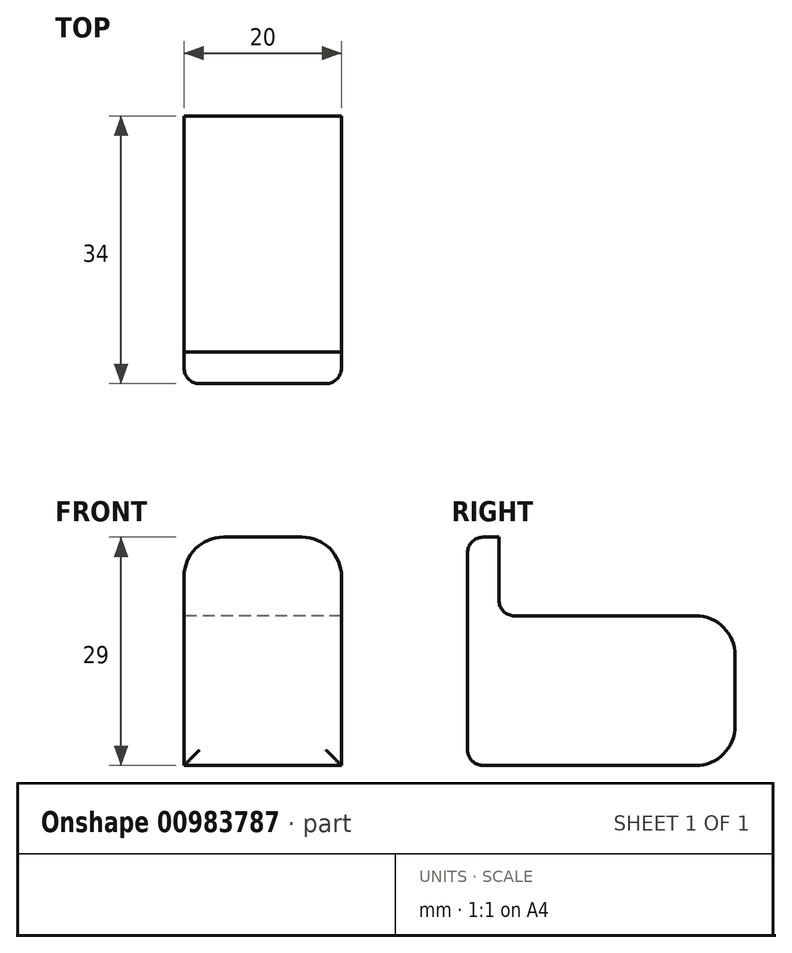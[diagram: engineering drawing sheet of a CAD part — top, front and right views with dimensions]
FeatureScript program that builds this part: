
annotation { "Feature Type Name" : "Feature", "Feature Type Description" : "" }
export const myFeature = defineFeature(function(context is Context, id is Id, definition is map)
    precondition{}
    {
        {
            var Q0;
            Q0=qCreatedBy(makeId("Right.planeOp"),FACE);
            var sketch = newSketch(context, id + "F0", { "sketchPlane" : qUnion([Q0])});
            skLineSegment(sketch, "E0", {"start": v(-17, 0) * mm, "end": v(-17, 29) * mm});
            skLineSegment(sketch, "E1", {"start": v(-17, 29) * mm, "end": v(-13, 29) * mm});
            skLineSegment(sketch, "E2", {"start": v(-13, 29) * mm, "end": v(-13, 19) * mm});
            skLineSegment(sketch, "E3", {"start": v(-13, 19) * mm, "end": v(17, 19) * mm});
            skLineSegment(sketch, "E4", {"start": v(17, 19) * mm, "end": v(17, 0) * mm});
            skLineSegment(sketch, "E5", {"start": v(17, 0) * mm, "end": v(-17, 0) * mm});
            skSolve(sketch);
        }
        {
            var Q0;
            Q0=makeQuery(id+"F0.imprint","IMPRINT",FACE,{"disambiguationData":[TD([[makeQuery(id+"F0.imprint","IMPRINT",EDGE,{"derivedFrom":sQuery(id+"F0.wireOp",EDGE,"E0")}),-1.0]])]});
            extrude(context, id + "F1", {"entities" : qUnion([Q0]), "depth" : 20 * mm, "offsetDistance" : 25 * mm});
        }
        {
            var Q0;
            Q0=makeQuery(id+"F1.opExtrude","CAP_EDGE",EDGE,{"disambiguationData":[OSD([sQuery(id+"F0.wireOp",EDGE,"E1")])],"isStart":false});
            var Q1;
            Q1=makeQuery(id+"F1.opExtrude","CAP_EDGE",EDGE,{"disambiguationData":[OSD([sQuery(id+"F0.wireOp",EDGE,"E1")])],"isStart":true});
            var Q2;
            Q2=makeQuery(id+"F1.opExtrude","SWEPT_EDGE",EDGE,{"disambiguationData":[OSD([sQuery(id+"F0.wireOp",EDGE,"E3"),sQuery(id+"F0.wireOp",EDGE,"E4")])]});
            var Q3;
            Q3=makeQuery(id+"F1.opExtrude","SWEPT_EDGE",EDGE,{"disambiguationData":[OSD([sQuery(id+"F0.wireOp",EDGE,"E4"),sQuery(id+"F0.wireOp",EDGE,"E5")])]});
            fillet(context, id + "F2", {"entities" : qUnion([Q0, Q1, Q2, Q3]), "radius" : 5 * mm, "tangentPropagation" : true, "allowEdgeOverflow" : false});
        }
        {
            var Q0;
            Q0=makeQuery(id+"F1.opExtrude","SWEPT_EDGE",EDGE,{"disambiguationData":[OSD([sQuery(id+"F0.wireOp",EDGE,"E0"),sQuery(id+"F0.wireOp",EDGE,"E5")])]});
            var Q1;
            Q1=makeQuery(id+"F1.opExtrude","SWEPT_EDGE",EDGE,{"disambiguationData":[OSD([sQuery(id+"F0.wireOp",EDGE,"E0"),sQuery(id+"F0.wireOp",EDGE,"E1")])]});
            var Q2;
            Q2=makeQuery(id+"F1.opExtrude","SWEPT_EDGE",EDGE,{"disambiguationData":[OSD([sQuery(id+"F0.wireOp",EDGE,"E2"),sQuery(id+"F0.wireOp",EDGE,"E3")])]});
            fillet(context, id + "F3", {"entities" : qUnion([Q0, Q1, Q2]), "radius" : 2 * mm, "tangentPropagation" : true, "allowEdgeOverflow" : false});
        }
    });
